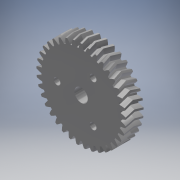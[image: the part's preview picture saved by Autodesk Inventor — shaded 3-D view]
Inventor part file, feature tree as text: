
AUTODESK INVENTOR PART (.ipt)
format: ipt  version: 2019 (Build 230136000, 136)  size: 911,360 bytes
history: native  units: mm (DEFAULTED — no unit token found)
features: sketch x4, plane x3, other x3, extrude x2, mirror x1, hole x1
ambient origin geometry x8: Origin, YZ Plane, XZ Plane, XY Plane, X Axis, Y Axis, Z Axis, Center Point
bodies: Solid1 (feature_tree)
feature tree (14):
  extrude  "Extrusion1"  Depth=5.0mm TaperAngle=0.0deg
  plane  "Work Plane2"
  plane  "Work Plane8"
  plane  "Work Plane9"
  other  "Spur Gear"
  mirror  "Mirror1"
  extrude  "Extrusion4"  Depth=10.0mm TaperAngle=0.0deg
  hole  "Hole4"  [1 undecoded]
  sketch  "Sketch1"  dims[d0=50.240958mm d1=5.0mm d2=0.0mm]
  sketch  "Sketch2"  dims[d3=47.741935mm d4=10.0mm d5=0.0mm]
  other  "Srf1"
  sketch  "Sketch6"  dims[d16=40.0mm d17=0.0mm d34=0.849079mm]
  sketch  "Sketch9"  dims[d39=0.0mm d41=0.0mm d43=40.0mm d46=40.0mm d47=0.0mm d48=0.0mm d66=7.5mm d67=5.0mm d68=0.0mm d92=27.0mm d93=30.0mm d95=360.0deg d97=3.75mm d98=6.0mm d99=6.5mm d100=6.0mm d101=14.835299mm d102=6.0mm d103=90.0deg]
  other  "Pitch Diameter"
note: 1 required parameter value undecoded (feature->parameter linkage not recoverable at this tier; creation-order binding heuristic only, values carry confidence <= 0.55)
